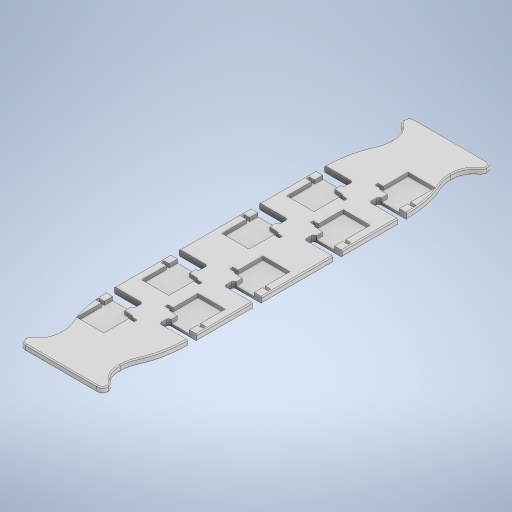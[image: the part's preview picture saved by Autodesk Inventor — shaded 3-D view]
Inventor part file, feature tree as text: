
AUTODESK INVENTOR PART (.ipt)
format: ipt  version: 2023.1 (Build 271208000, 208)  size: 706,048 bytes
history: native  units: mm
features: extrude x3, other x2, fillet x2
ambient origin geometry x8: Origin, YZ Plane, XZ Plane, XY Plane, X Axis, Y Axis, Z Axis, Center Point
bodies: Solid1 (feature_tree)
feature tree (7):
  extrude  "Baseplate"  Depth=70.0mm
  other  "Servo Feature Layout"
  extrude  "Horn Clearance Slot"  Depth=250.0mm
  extrude  "Servo Mount Pockets"  Depth=5.0mm TaperAngle=0.0deg
  fillet  "Fillets (Baseplate)"  Radius=34.0mm
  fillet  "Fillets (Clearance Slot)"  Radius=55.0mm
  other  "Baseplate Profile"
